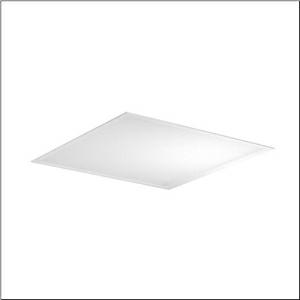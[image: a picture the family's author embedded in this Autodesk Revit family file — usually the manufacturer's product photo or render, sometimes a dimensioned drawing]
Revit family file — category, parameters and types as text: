
# Revit family: apollon_21_square_51mq12w72m14
name_source: partatom
category: Lighting Fixtures
units: mm (PartAtom-declared; Revit-internal decimal feet)

## family parameters
Cut with Voids When Loaded = No
Host = Face
Light Source = No
Part Type = Normal
Room Calculation Point = No
Round Connector Dimension = Use Diameter
Shared = No

## types (1)
- --- (1 x LED, 4200 lm, 24.2 W, 4000K)
    Apparent Load = 24 VA
    CIE Flux Codes = 60 87 97 100 100
    Color Rendering = 80
    Color Temperature = 4000K
    Default Elevation = 1800 mm
    Description = Apollon 21 square, office luminaire, primary optical cover: micro prismatic cover, of PMMA, CAT 2 (L<= 3000cd/m²), light emission: direct distribution, primary light characteristic: symmetric, installation type: lay-in mounting, LED, rated luminous flux: 4.200lm, luminous efficacy: 174lm/W, light colour: 830/840, colour temperature: 3000/4000K, control gear: ON/OFF, with terminal, 3-pole, mains connection: 220..240V, AC/DC, 0/50..60Hz, rated input power: 24.2W, housing, of aluminium, coated, traffic white (RAL 9016), module: M600, length: 595mm, width: 595mm, height: 55mm, recess depth: 180mm, housing upper side, of sheet steel, galvanised, protection rating (complete): IP20, protection rating (lamp compartment, on room side): IP50, insulation class (complete): insulation class II (safety insulation), certification: CE, ENEC, impact resistance: IK03, permissible operating ambient temperature: -20..+45°C, permissible storage temperature: -40..+80°C, standard: EN 60598-2-22, packaging unit: 1 piece
    Height = 0 mm  [stored 0 ft]
    Lamp = 1 x LED
    Lamp Light Flux = 4200 lm
    Lamp Power = 24.2 W
    Lamp count = 1
    Length = 595 mm
    Luminous efficacy = 174 lm/W
    Manufacturer = Siteco
    ModVariant = No
    Model = 51MQ12W72M14
    Mounting Place = Ceiling
    Mounting Type = Recessed
    Number of Poles = 1
    OnlyDefault = Yes
    Power Factor = 1
    Product Name = Apollon 21 square
    Product group = office luminaire | ceiling recessed
    ProductGroupID = 401
    Protection Class = Protection class II
    Protection Degree = IP 20
    RLX_Detail_Level = 1
    RLX_Emergency_Light_Flux = 0 lm
    RLX_Emergency_Type = 0
    RLX_Emergency_Type_DB = No
    RlxData = <blob elided: 12777 chars, md5=e3ada804>
    Socket = socket
    Standby Power = 0 W
    System Light Flux = 4200 lm
    System Power = 24 W
    Type Comments = factory setting
    Type Image = l_1291049.jpg
    URL = http://relux.com
    VarID = @adj_068448
    Voltage = 0 V
    Weight = 0.00 kg
    Width = 595 mm

note: [stored X ft] marks values corroborated as IEEE doubles in the binary element streams (Revit-internal decimal feet)

## geometry (parser evidence)
native form markers: Sweep x8
no freeform markers — native parametric forms only
